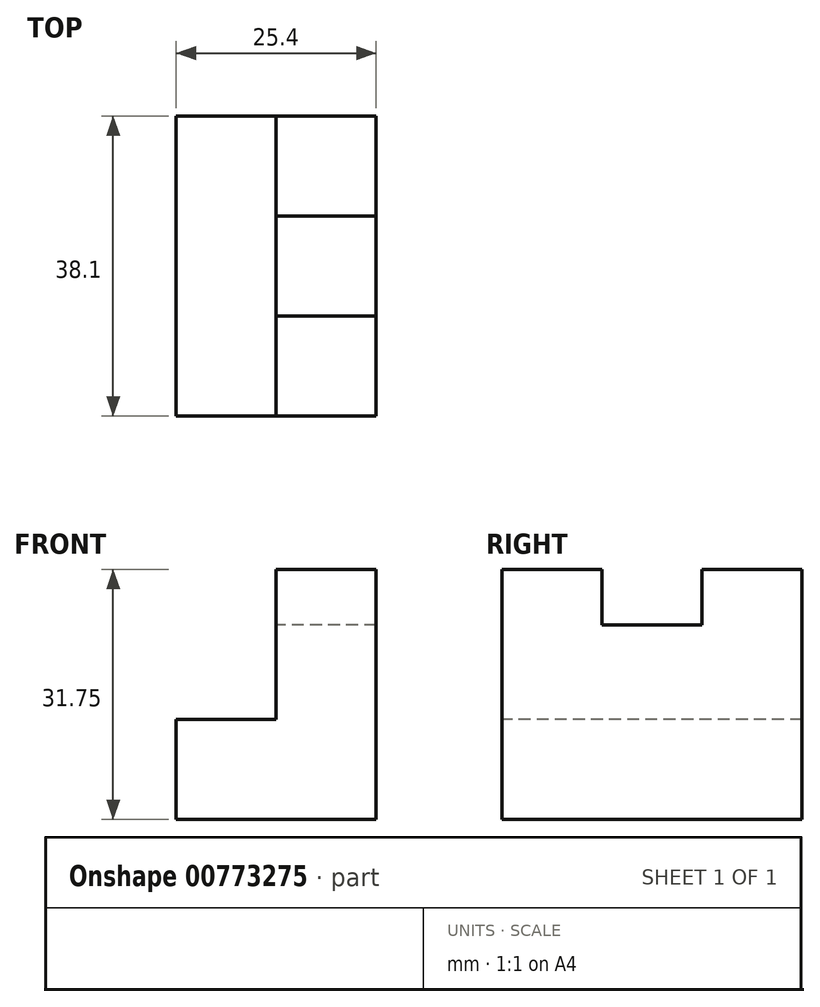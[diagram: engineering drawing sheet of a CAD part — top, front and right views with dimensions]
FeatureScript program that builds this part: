
annotation { "Feature Type Name" : "Feature", "Feature Type Description" : "" }
export const myFeature = defineFeature(function(context is Context, id is Id, definition is map)
    precondition{}
    {
        {
            var Q0;
            Q0=qCreatedBy(makeId("Right.planeOp"),FACE);
            var sketch = newSketch(context, id + "F0", { "sketchPlane" : qUnion([Q0])});
            skLineSegment(sketch, "E0", {"start": v(0, 0) * mm, "end": v(-38.1, 0) * mm});
            skLineSegment(sketch, "E1", {"start": v(-38.1, 0) * mm, "end": v(-38.1, 31.75) * mm});
            skLineSegment(sketch, "E2", {"start": v(-38.1, 31.75) * mm, "end": v(0, 31.75) * mm});
            skLineSegment(sketch, "E3", {"start": v(0, 0) * mm, "end": v(0, 31.75) * mm});
            skSolve(sketch);
        }
        {
            var Q0;
            Q0=makeQuery(id+"F0.imprint","IMPRINT",FACE,{"disambiguationData":[TD([[makeQuery(id+"F0.imprint","IMPRINT",EDGE,{"derivedFrom":sQuery(id+"F0.wireOp",EDGE,"E0")}),-1.0]])]});
            extrude(context, id + "F1", {"entities" : qUnion([Q0]), "depth" : 25.4 * mm, "offsetDistance" : 25.4 * mm});
        }
        {
            var Q0;
            Q0=makeQuery(id+"F1.opExtrude","SWEPT_FACE",FACE,{"disambiguationData":[OSD([sQuery(id+"F0.wireOp",EDGE,"E1")])]});
            var sketch = newSketch(context, id + "F2", { "sketchPlane" : qUnion([Q0])});
            skLineSegment(sketch, "E4", {"start": v(0, 0) * mm, "end": v(0, 12.7) * mm});
            skLineSegment(sketch, "E5", {"start": v(0, 12.7) * mm, "end": v(12.7, 12.7) * mm});
            skLineSegment(sketch, "E6", {"start": v(12.7, 12.7) * mm, "end": v(12.7, 31.75) * mm});
            skSolve(sketch);
        }
        {
            var Q0;
            {var subQ0=sQuery(id+"F2.wireOp",EDGE,"E5");Q0=makeQuery(id+"F2.imprint","IMPRINT",FACE,{"disambiguationData":[TD([[makeQuery(id+"F2.imprint","IMPRINT",EDGE,{"derivedFrom":subQ0}),1.0]])]});}
            extrude(context, id + "F3", {"entities" : qUnion([Q0]), "operationType" : NewBodyOperationType.REMOVE, "oppositeDirection" : true, "depth" : 38.1 * mm, "offsetDistance" : 25.4 * mm});
        }
        {
            var Q0;
            Q0=makeQuery(id+"F3.boolean.opBoolean","COPY",FACE,{"derivedFrom":makeQuery(id+"F3.opExtrude","SWEPT_FACE",FACE,{"disambiguationData":[OSD([sQuery(id+"F2.wireOp",EDGE,"E6")])]})});
            var sketch = newSketch(context, id + "F4", { "sketchPlane" : qUnion([Q0])});
            skLineSegment(sketch, "E7", {"start": v(0, 31.75) * mm, "end": v(12.7, 31.75) * mm});
            skLineSegment(sketch, "E8", {"start": v(38.1, 31.75) * mm, "end": v(25.4, 31.75) * mm});
            skLineSegment(sketch, "E9", {"start": v(25.4, 31.75) * mm, "end": v(25.4, 24.7) * mm});
            skLineSegment(sketch, "E10", {"start": v(25.4, 24.7) * mm, "end": v(12.7, 24.7) * mm});
            skLineSegment(sketch, "E11", {"start": v(12.7, 31.75) * mm, "end": v(12.7, 24.7) * mm});
            skSolve(sketch);
        }
        {
            var Q0;
            {var subQ0=sQuery(id+"F4.wireOp",EDGE,"E9");Q0=makeQuery(id+"F4.imprint","IMPRINT",FACE,{"disambiguationData":[TD([[makeQuery(id+"F4.imprint","IMPRINT",EDGE,{"derivedFrom":subQ0}),-1.0]])]});}
            extrude(context, id + "F5", {"entities" : qUnion([Q0]), "operationType" : NewBodyOperationType.REMOVE, "oppositeDirection" : true, "depth" : 25.4 * mm, "offsetDistance" : 25.4 * mm});
        }
    });
